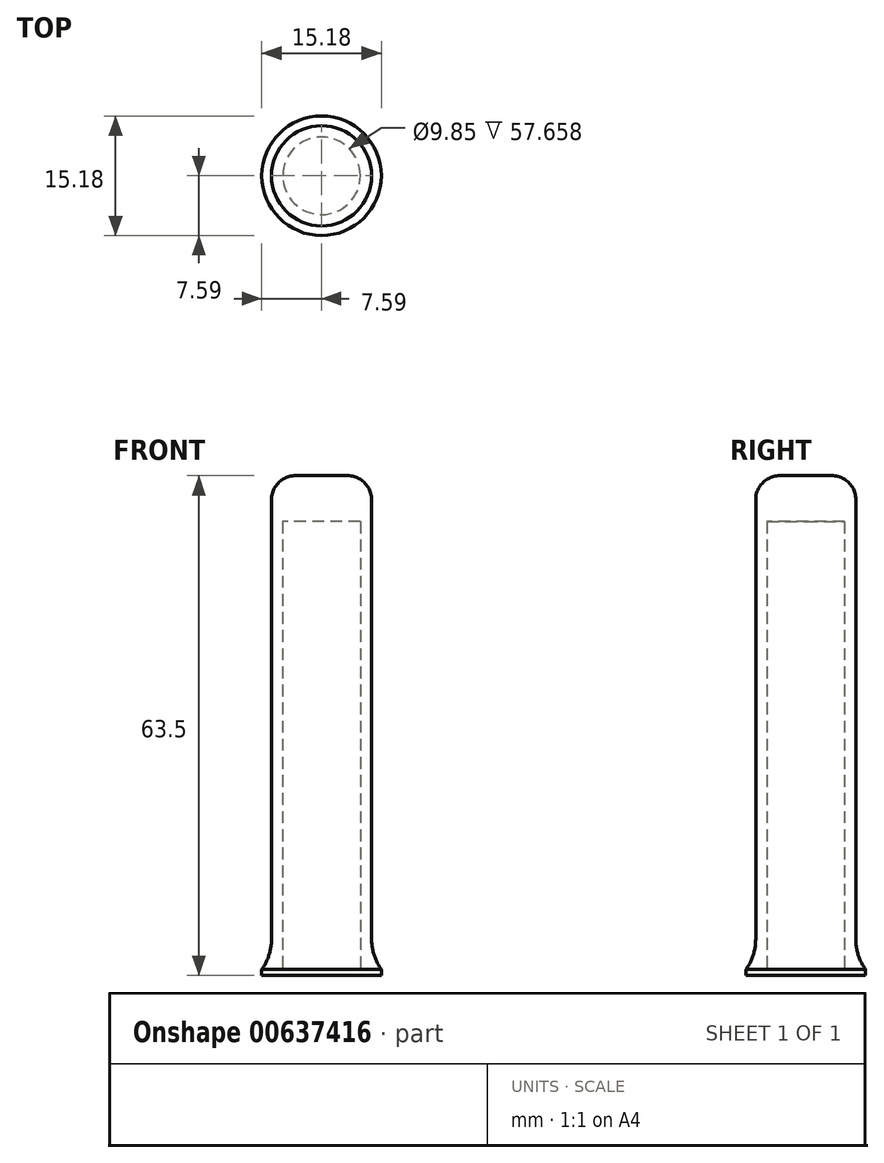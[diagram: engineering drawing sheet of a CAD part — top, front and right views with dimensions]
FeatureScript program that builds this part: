
annotation { "Feature Type Name" : "Feature", "Feature Type Description" : "" }
export const myFeature = defineFeature(function(context is Context, id is Id, definition is map)
    precondition{}
    {
        {
            var Q0;
            Q0=qCreatedBy(makeId("Top.planeOp"),FACE);
            var sketch = newSketch(context, id + "F0", { "sketchPlane" : qUnion([Q0])});
            skCircle(sketch, "E0", {"center": v(0, 0) * mm, "radius": 6.36 * mm});
            skSolve(sketch);
        }
        {
            var Q0;
            Q0=makeQuery(id+"F0.imprint","IMPRINT",FACE,{"disambiguationData":[TD([[makeQuery(id+"F0.imprint","IMPRINT",EDGE,{"derivedFrom":sQuery(id+"F0.wireOp",EDGE,"E0")}),1.0]])]});
            extrude(context, id + "F1", {"entities" : qUnion([Q0]), "depth" : 63.5 * mm, "offsetDistance" : 25.4 * mm});
        }
        {
            var Q0;
            Q0=makeQuery(id+"F1.opExtrude","CAP_FACE",FACE,{"disambiguationData":[OSD([sQuery(id+"F0.wireOp",EDGE,"E0")])],"isStart":true});
            var sketch = newSketch(context, id + "F2", { "sketchPlane" : qUnion([Q0])});
            skCircle(sketch, "E1", {"center": v(0, 0) * mm, "radius": 4.76 * mm});
            skSolve(sketch);
        }
        {
            var Q0;
            Q0=makeQuery(id+"F2.imprint","IMPRINT",FACE,{"disambiguationData":[TD([[makeQuery(id+"F2.imprint","IMPRINT",EDGE,{"derivedFrom":sQuery(id+"F2.wireOp",EDGE,"E1")}),1.0]])]});
            extrude(context, id + "F3", {"entities" : qUnion([Q0]), "operationType" : NewBodyOperationType.REMOVE, "oppositeDirection" : true, "depth" : 25.15 * mm, "offsetDistance" : 25.4 * mm});
        }
        {
            var Q0;
            Q0=qCreatedBy(makeId("Top.planeOp"),FACE);
            var sketch = newSketch(context, id + "F4", { "sketchPlane" : qUnion([Q0])});
            skCircle(sketch, "E2", {"center": v(0, 0) * mm, "radius": 7.6 * mm});
            skSolve(sketch);
        }
        {
            var Q0;
            Q0 = qSketchRegion(id + "F4", true);
            extrude(context, id + "F5", {"entities" : qUnion([Q0]), "operationType" : NewBodyOperationType.ADD, "depth" : 0.79 * mm, "offsetDistance" : 25.4 * mm});
        }
        {
            var Q0;
            Q0=makeQuery(id+"F5.boolean.opBoolean","MERGE",FACE,{"derivedFrom":[makeQuery(id+"F1.opExtrude","CAP_FACE",FACE,{"disambiguationData":[OSD([sQuery(id+"F0.wireOp",EDGE,"E0")])],"isStart":true}),makeQuery(id+"F5.opExtrude","CAP_FACE",FACE,{"disambiguationData":[OSD([sQuery(id+"F4.wireOp",EDGE,"E2")])],"isStart":true})]});
            var sketch = newSketch(context, id + "F6", { "sketchPlane" : qUnion([Q0])});
            skCircle(sketch, "E3", {"center": v(0, 0) * mm, "radius": 4.75 * mm});
            skSolve(sketch);
        }
        {
            var Q0;
            Q0=makeQuery(id+"F6.imprint","IMPRINT",FACE,{"disambiguationData":[TD([[makeQuery(id+"F6.imprint","IMPRINT",EDGE,{"derivedFrom":sQuery(id+"F6.wireOp",EDGE,"E3")}),1.0]])]});
            extrude(context, id + "F7", {"entities" : qUnion([Q0]), "operationType" : NewBodyOperationType.REMOVE, "oppositeDirection" : true, "depth" : 35.3 * mm, "offsetDistance" : 25.4 * mm});
        }
        {
            var Q0;
            Q0=makeQuery(id+"F1.opExtrude","CAP_EDGE",EDGE,{"disambiguationData":[OSD([sQuery(id+"F0.wireOp",EDGE,"E0")])],"isStart":false});
            fillet(context, id + "F8", {"entities" : qUnion([Q0]), "radius" : 3.07 * mm, "tangentPropagation" : true, "allowEdgeOverflow" : false});
        }
        {
            var Q0;
            Q0=makeQuery(id+"F5.boolean.opBoolean","INTERSECT",EDGE,{"derivedFrom":[makeQuery(id+"F1.opExtrude","SWEPT_FACE",FACE,{"disambiguationData":[OSD([sQuery(id+"F0.wireOp",EDGE,"E0")])]}),makeQuery(id+"F5.opExtrude","CAP_FACE",FACE,{"disambiguationData":[OSD([sQuery(id+"F4.wireOp",EDGE,"E2")])],"isStart":false})]});
            fillet(context, id + "F9", {"entities" : qUnion([Q0]), "radius" : 6.44 * mm, "tangentPropagation" : true, "allowEdgeOverflow" : false});
        }
        {
            var Q0;
            Q0=qCreatedBy(makeId("Top.planeOp"),FACE);
            var sketch = newSketch(context, id + "F10", { "sketchPlane" : qUnion([Q0])});
            skCircle(sketch, "E4", {"center": v(0, 0) * mm, "radius": 4.93 * mm});
            skSolve(sketch);
        }
        {
            var Q0;
            Q0 = qSketchRegion(id + "F10", true);
            extrude(context, id + "F11", {"entities" : qUnion([Q0]), "operationType" : NewBodyOperationType.REMOVE, "depth" : 57.66 * mm, "offsetDistance" : 25.4 * mm});
        }
    });
